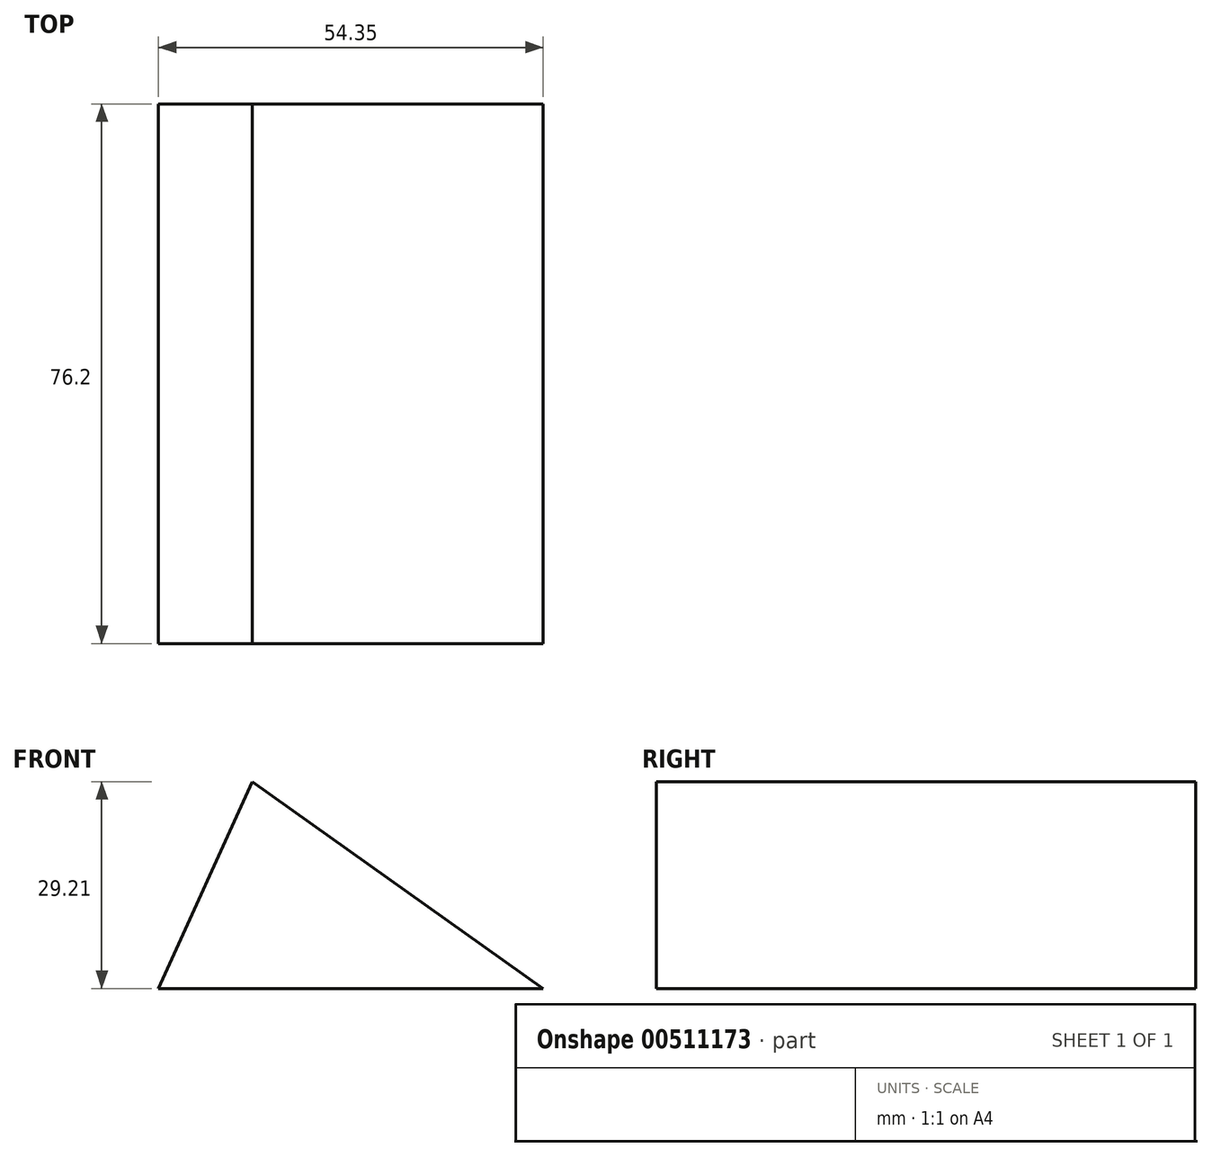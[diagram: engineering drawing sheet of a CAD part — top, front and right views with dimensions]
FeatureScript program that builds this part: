
annotation { "Feature Type Name" : "Feature", "Feature Type Description" : "" }
export const myFeature = defineFeature(function(context is Context, id is Id, definition is map)
    precondition{}
    {
        {
            var Q0;
            Q0=qCreatedBy(makeId("Front.planeOp"),FACE);
            var sketch = newSketch(context, id + "F0", { "sketchPlane" : qUnion([Q0])});
            skLineSegment(sketch, "E0", {"start": v(-12.24, 18.78) * mm, "end": v(-25.53, -10.43) * mm});
            skLineSegment(sketch, "E1", {"start": v(-25.53, -10.43) * mm, "end": v(28.82, -10.43) * mm});
            skLineSegment(sketch, "E2", {"start": v(28.82, -10.43) * mm, "end": v(-12.24, 18.78) * mm});
            skLineSegment(sketch, "E3", {"start": v(-12.24, 18.78) * mm, "end": v(-12.24, -10.43) * mm});
            skSolve(sketch);
        }
        {
            var Q0;
            {var subQ0=sQuery(id+"F0.wireOp",EDGE,"E2");Q0=makeQuery(id+"F0.imprint","IMPRINT",FACE,{"disambiguationData":[TD([[makeQuery(id+"F0.imprint","IMPRINT",EDGE,{"derivedFrom":subQ0}),1.0]])]});}
            var Q1;
            {var subQ0=sQuery(id+"F0.wireOp",EDGE,"E0");Q1=makeQuery(id+"F0.imprint","IMPRINT",FACE,{"disambiguationData":[TD([[makeQuery(id+"F0.imprint","IMPRINT",EDGE,{"derivedFrom":subQ0}),1.0]])]});}
            extrude(context, id + "F1", {"entities" : qUnion([Q0, Q1]), "depth" : 76.2 * mm});
        }
    });
